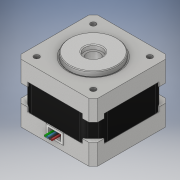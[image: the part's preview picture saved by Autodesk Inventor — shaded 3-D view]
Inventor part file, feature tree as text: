
AUTODESK INVENTOR PART (.ipt)
format: ipt  version: 2019.4 (Build 234330000, 330)  size: 406,528 bytes
history: native  units: mm
features: sketch x13, extrude x11, fillet x3, hole x2, chamfer x2, projected_geometry x2, other x1, pattern_circular x1
ambient origin geometry x8: Origin, YZ Plane, XZ Plane, XY Plane, X Axis, Y Axis, Z Axis, Center Point
bodies: Solide1 (feature_tree)
feature tree (35):
  extrude  "Extrusion1"  Depth=35.2mm
  hole  "Perçage1"  [1 undecoded]
  extrude  "Extrusion2"  Depth=2.0mm
  chamfer  "Chanfrein1"  Distance=2.0mm
  extrude  "Extrusion3"  Depth=2.0mm
  chamfer  "Chanfrein2"  Distance=2.0mm
  extrude  "Extrusion4"  Depth=2.0mm
  extrude  "Extrusion5"  Depth=2.0mm
  fillet  "Congé1"  Radius=2.0mm
  other  "Plan de construction1"
  extrude  "Extrusion6"  Depth=2.0mm
  extrude  "Extrusion8"  Depth=27.0mm TaperAngle=0.0deg
  pattern_circular  "Réseau circulaire1"  [2 undecoded]
  fillet  "Congé2"  Radius=26.0mm
  extrude  "Extrusion9"  Depth=22.0mm
  hole  "Perçage3"  [1 undecoded]
  fillet  "Congé3"  Radius=0.3mm
  extrude  "Extrusion10"  Depth=23.5mm
  extrude  "Extrusion11"  Depth=0.2mm TaperAngle=0.0deg
  extrude  "Extrusion12"  Depth=0.2mm
  sketch  "Esquisse1"
  sketch  "Esquisse2"
  sketch  "Esquisse3"
  sketch  "Esquisse4"
  sketch  "Esquisse5"
  sketch  "Esquisse6"
  sketch  "Esquisse7"
  projected_geometry  "Boucle projetée1"
  sketch  "Esquisse9"
  sketch  "Esquisse10"
  sketch  "Esquisse12"
  sketch  "Esquisse13"
  sketch  "Esquisse14"
  projected_geometry  "Boucle projetée2"
  sketch  "Esquisse15"
note: 4 required parameter values undecoded (feature->parameter linkage not recoverable at this tier; creation-order binding heuristic only, values carry confidence <= 0.55)
